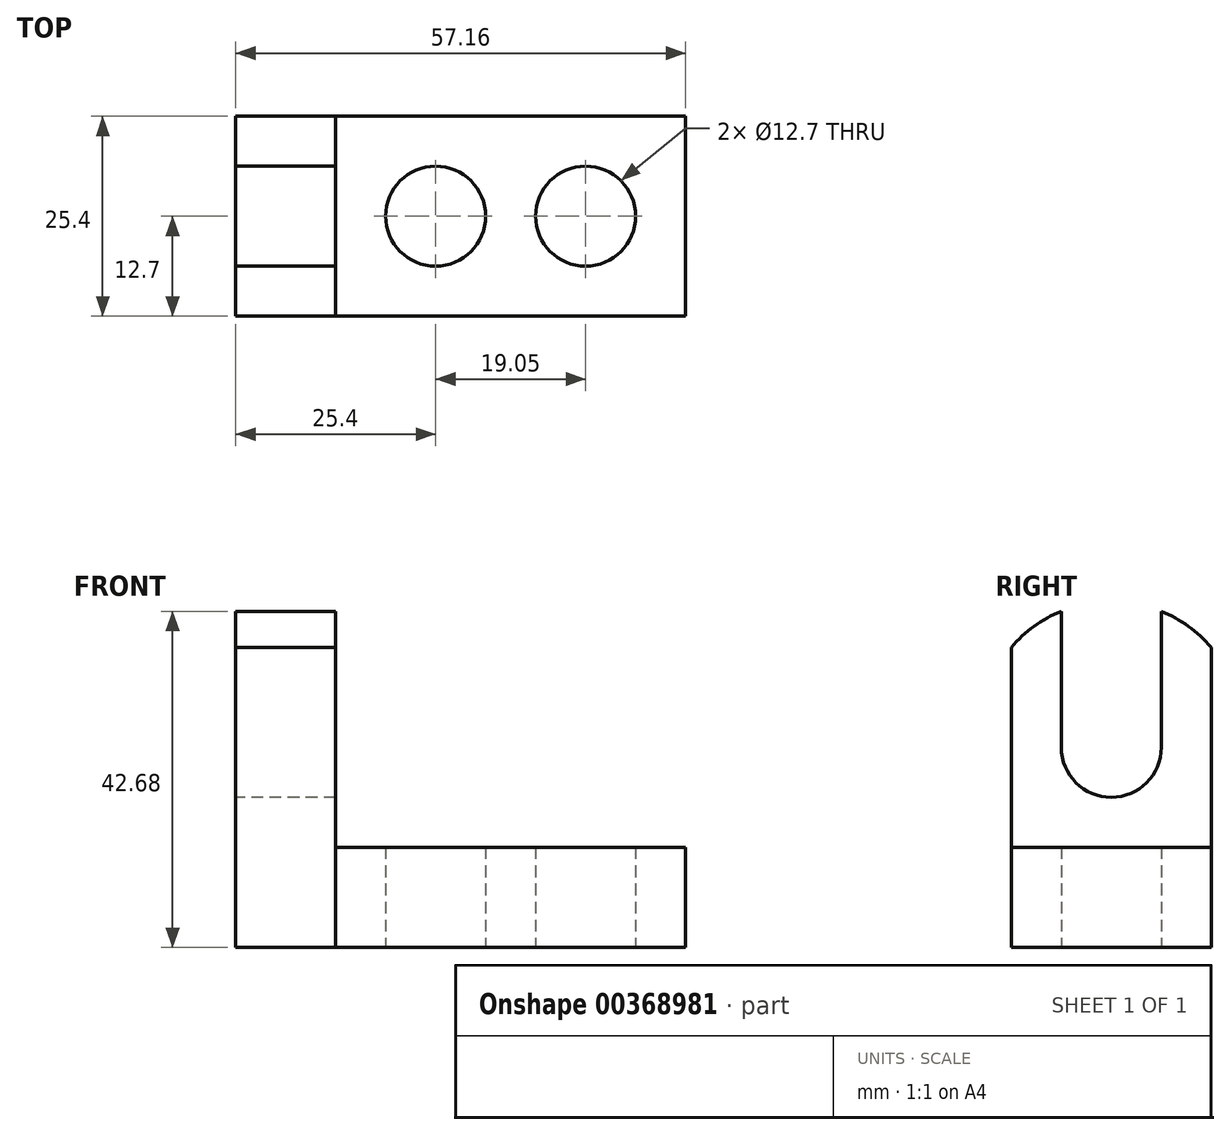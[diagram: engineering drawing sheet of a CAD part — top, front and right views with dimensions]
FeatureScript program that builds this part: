
annotation { "Feature Type Name" : "Feature", "Feature Type Description" : "" }
export const myFeature = defineFeature(function(context is Context, id is Id, definition is map)
    precondition{}
    {
        {
            var Q0;
            Q0=qCreatedBy(makeId("Right.planeOp"),FACE);
            var sketch = newSketch(context, id + "F0", { "sketchPlane" : qUnion([Q0])});
            skLineSegment(sketch, "E0", {"start": v(0, 0) * mm, "end": v(-25.4, 0) * mm});
            skLineSegment(sketch, "E1", {"start": v(-25.4, 0) * mm, "end": v(-25.4, 44.45) * mm});
            skLineSegment(sketch, "E2", {"start": v(-25.4, 44.45) * mm, "end": v(0, 44.45) * mm});
            skLineSegment(sketch, "E3", {"start": v(0, 44.45) * mm, "end": v(0, 0) * mm});
            skLineSegment(sketch, "E4", {"start": v(-6.35, 44.45) * mm, "end": v(-6.35, 25.4) * mm});
            skLineSegment(sketch, "E5", {"start": v(-19.05, 44.45) * mm, "end": v(-19.05, 25.4) * mm});
            skCircle(sketch, "E6", {"center": v(-12.7, 25.4) * mm, "radius": 6.35 * mm});
            skPoint(sketch, "E6.third.point", {"position": v(-6.35, 25.4) * mm});
            skPoint(sketch, "E7.first.point", {"position": v(0, 34.93) * mm});
            skPoint(sketch, "E7.first.point.positionSnap0", {"position": v(-6.35, 34.93) * mm});
            skPoint(sketch, "E7.second.point", {"position": v(-25.4, 38.1) * mm});
            skPoint(sketch, "E7.third.point", {"position": v(-12.7, 44.45) * mm});
            skSolve(sketch);
        }
        {
            var Q0;
            Q0=makeQuery(id+"F0.imprint","IMPRINT",FACE,{"disambiguationData":[TD([[makeQuery(id+"F0.imprint","IMPRINT",EDGE,{"derivedFrom":sQuery(id+"F0.wireOp",EDGE,"E0")}),-1.0]])]});
            extrude(context, id + "F1", {"entities" : qUnion([Q0]), "depth" : 12.7 * mm});
        }
        {
            var Q0;
            Q0=qCreatedBy(makeId("Top.planeOp"),FACE);
            var sketch = newSketch(context, id + "F2", { "sketchPlane" : qUnion([Q0])});
            skLineSegment(sketch, "E8", {"start": v(12.71, 0) * mm, "end": v(12.71, -25.4) * mm});
            skLineSegment(sketch, "E9", {"start": v(12.71, -25.4) * mm, "end": v(57.16, -25.4) * mm});
            skLineSegment(sketch, "E10", {"start": v(57.16, -25.4) * mm, "end": v(57.16, 0) * mm});
            skLineSegment(sketch, "E11", {"start": v(57.16, 0) * mm, "end": v(12.71, 0) * mm});
            skSolve(sketch);
        }
        {
            var Q0;
            Q0=makeQuery(id+"F2.imprint","IMPRINT",FACE,{"disambiguationData":[TD([[makeQuery(id+"F2.imprint","IMPRINT",EDGE,{"derivedFrom":sQuery(id+"F2.wireOp",EDGE,"E8")}),1.0]])]});
            extrude(context, id + "F3", {"entities" : qUnion([Q0]), "depth" : 12.7 * mm});
        }
        {
            var Q0;
            Q0=qCreatedBy(makeId("Top.planeOp"),FACE);
            var sketch = newSketch(context, id + "F4", { "sketchPlane" : qUnion([Q0])});
            skCircle(sketch, "E12", {"center": v(25.4, -12.7) * mm, "radius": 6.35 * mm});
            skPoint(sketch, "E12.first.point", {"position": v(19.2, -11.32) * mm});
            skPoint(sketch, "E12.second.point", {"position": v(30.94, -15.8) * mm});
            skPoint(sketch, "E12.third.point", {"position": v(24.54, -6.4) * mm});
            skCircle(sketch, "E13", {"center": v(44.45, -12.7) * mm, "radius": 6.35 * mm});
            skPoint(sketch, "E13.first.point", {"position": v(38.25, -11.35) * mm});
            skPoint(sketch, "E13.second.point", {"position": v(50.14, -15.51) * mm});
            skPoint(sketch, "E13.third.point", {"position": v(43, -18.88) * mm});
            skSolve(sketch);
        }
        {
            var Q0;
            Q0 = qSketchRegion(id + "F4", true);
            extrude(context, id + "F5", {"entities" : qUnion([Q0]), "operationType" : NewBodyOperationType.REMOVE, "depth" : 25.4 * mm});
        }
        {
            var Q0;
            Q0=makeQuery(id+"F1.opExtrude","CAP_FACE",FACE,{"disambiguationData":[OSD([sQuery(id+"F0.wireOp",EDGE,"E0"),sQuery(id+"F0.wireOp",EDGE,"E1"),sQuery(id+"F0.wireOp",EDGE,"E2"),sQuery(id+"F0.wireOp",EDGE,"E3"),sQuery(id+"F0.wireOp",EDGE,"E4"),sQuery(id+"F0.wireOp",EDGE,"E5"),sQuery(id+"F0.wireOp",EDGE,"E6")])],"isStart":true});
            var sketch = newSketch(context, id + "F6", { "sketchPlane" : qUnion([Q0])});
            skCircle(sketch, "E14", {"center": v(12.7, 27.2) * mm, "radius": 16.74 * mm});
            skPoint(sketch, "E14.first.point", {"position": v(0, 38.1) * mm});
            skPoint(sketch, "E14.second.point", {"position": v(25.4, 38.1) * mm});
            skPoint(sketch, "E14.third.point", {"position": v(11.3, 43.88) * mm});
            skSolve(sketch);
        }
        {
            var Q0;
            {var subQ4=sQuery(id+"F0.wireOp",EDGE,"E3");var subQ7=sQuery(id+"F0.wireOp",EDGE,"E2");var subQ8=makeQuery(id+"F1.opExtrude","CAP_EDGE",EDGE,{"disambiguationData":[OSD([subQ7]),TDD([makeQuery(id+"F0.imprint","IMPRINT",EDGE,{"disambiguationData":[TD([[makeQuery(id+"F0.imprint","INTERSECT",VERTEX,{"derivedFrom":[subQ7,subQ4]}),1.0]])],"derivedFrom":subQ7})])],"isStart":true});Q0=makeQuery(id+"F6.imprint","IMPRINT",FACE,{"disambiguationData":[TD([[makeQuery(id+"F6.imprint","IMPRINT",EDGE,{"derivedFrom":subQ8}),1.0]])]});}
            var Q1;
            {var subQ4=sQuery(id+"F0.wireOp",EDGE,"E1");var subQ7=sQuery(id+"F0.wireOp",EDGE,"E2");var subQ8=makeQuery(id+"F1.opExtrude","CAP_EDGE",EDGE,{"disambiguationData":[OSD([subQ7]),TDD([makeQuery(id+"F0.imprint","IMPRINT",EDGE,{"disambiguationData":[TD([[makeQuery(id+"F0.imprint","INTERSECT",VERTEX,{"derivedFrom":[subQ4,subQ7]}),-1.0]])],"derivedFrom":subQ7})])],"isStart":true});Q1=makeQuery(id+"F6.imprint","IMPRINT",FACE,{"disambiguationData":[TD([[makeQuery(id+"F6.imprint","IMPRINT",EDGE,{"derivedFrom":subQ8}),1.0]])]});}
            extrude(context, id + "F7", {"entities" : qUnion([Q0, Q1]), "operationType" : NewBodyOperationType.REMOVE, "oppositeDirection" : true, "depth" : 12.7 * mm});
        }
    });
